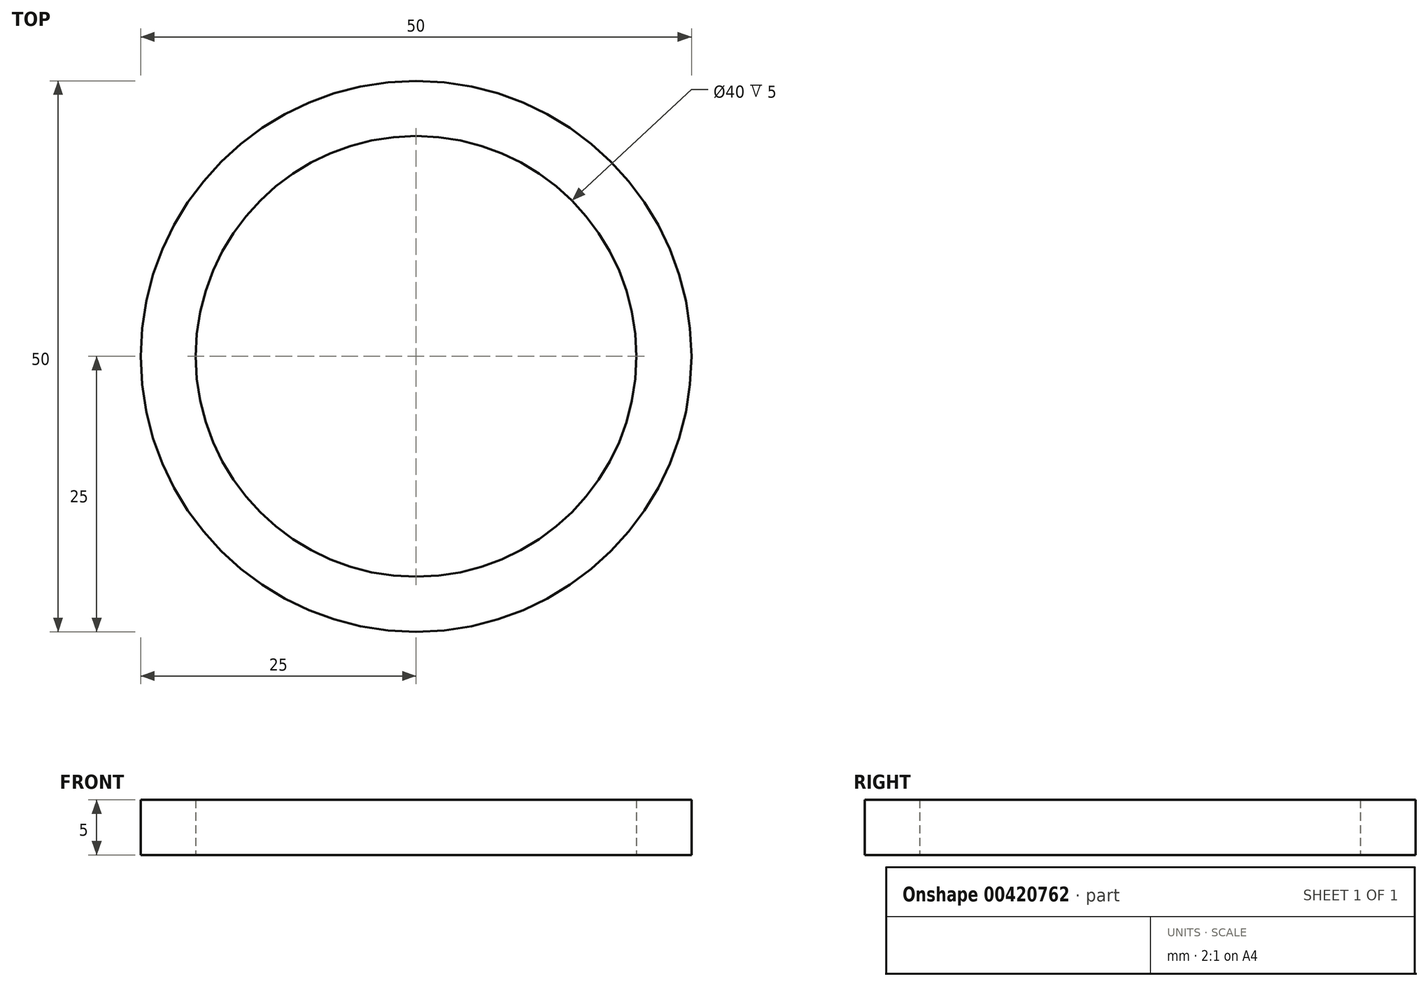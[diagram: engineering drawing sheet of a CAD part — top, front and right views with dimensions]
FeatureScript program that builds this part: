
annotation { "Feature Type Name" : "Feature", "Feature Type Description" : "" }
export const myFeature = defineFeature(function(context is Context, id is Id, definition is map)
    precondition{}
    {
        {
            var Q0;
            Q0=qCreatedBy(makeId("Top.planeOp"),FACE);
            var sketch = newSketch(context, id + "F0", { "sketchPlane" : qUnion([Q0])});
            skCircle(sketch, "E0", {"center": v(0, 0) * mm, "radius": 25 * mm});
            skCircle(sketch, "E1", {"center": v(0, 0) * mm, "radius": 20 * mm});
            skSolve(sketch);
        }
        {
            var Q0;
            Q0=makeQuery(id+"F0.imprint","IMPRINT",FACE,{"disambiguationData":[TD([[makeQuery(id+"F0.imprint","IMPRINT",EDGE,{"derivedFrom":sQuery(id+"F0.wireOp",EDGE,"E0")}),1.0]])]});
            extrude(context, id + "F1", {"entities" : qUnion([Q0]), "depth" : 5 * mm});
        }
    });
